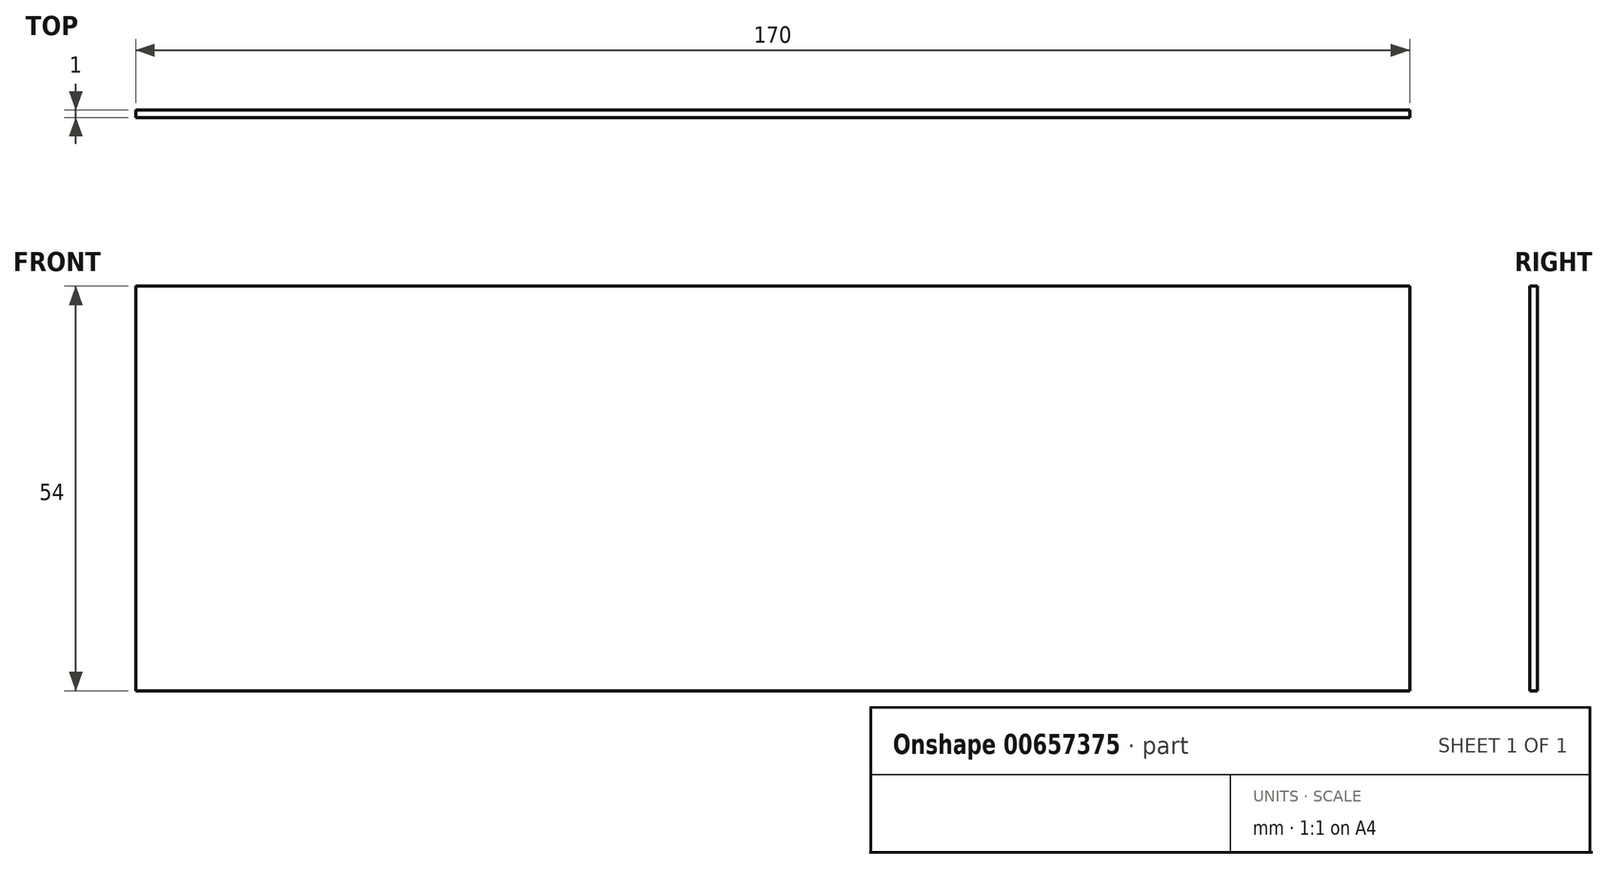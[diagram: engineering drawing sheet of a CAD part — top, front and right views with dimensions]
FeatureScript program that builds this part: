
annotation { "Feature Type Name" : "Feature", "Feature Type Description" : "" }
export const myFeature = defineFeature(function(context is Context, id is Id, definition is map)
    precondition{}
    {
        {
            var Q0;
            Q0=qCreatedBy(makeId("Front.planeOp"),FACE);
            var sketch = newSketch(context, id + "F0", { "sketchPlane" : qUnion([Q0])});
            skLineSegment(sketch, "E0.bottom", {"start": v(85, 27) * mm, "end": v(-85, 27) * mm});
            skLineSegment(sketch, "E0.top", {"start": v(85, -27) * mm, "end": v(-85, -27) * mm});
            skLineSegment(sketch, "E0.left", {"start": v(85, 27) * mm, "end": v(85, -27) * mm});
            skLineSegment(sketch, "E0.right", {"start": v(-85, 27) * mm, "end": v(-85, -27) * mm});
            skPoint(sketch, "E0.middle", {"position": v(0, 0) * mm});
            skSolve(sketch);
        }
        {
            var Q0;
            Q0=makeQuery(id+"F0.imprint","IMPRINT",FACE,{"disambiguationData":[TD([[makeQuery(id+"F0.imprint","IMPRINT",EDGE,{"derivedFrom":sQuery(id+"F0.wireOp",EDGE,"E0.bottom")}),1.0]])]});
            extrude(context, id + "F1", {"entities" : qUnion([Q0]), "depth" : 1 * mm, "offsetDistance" : 25 * mm});
        }
    });
